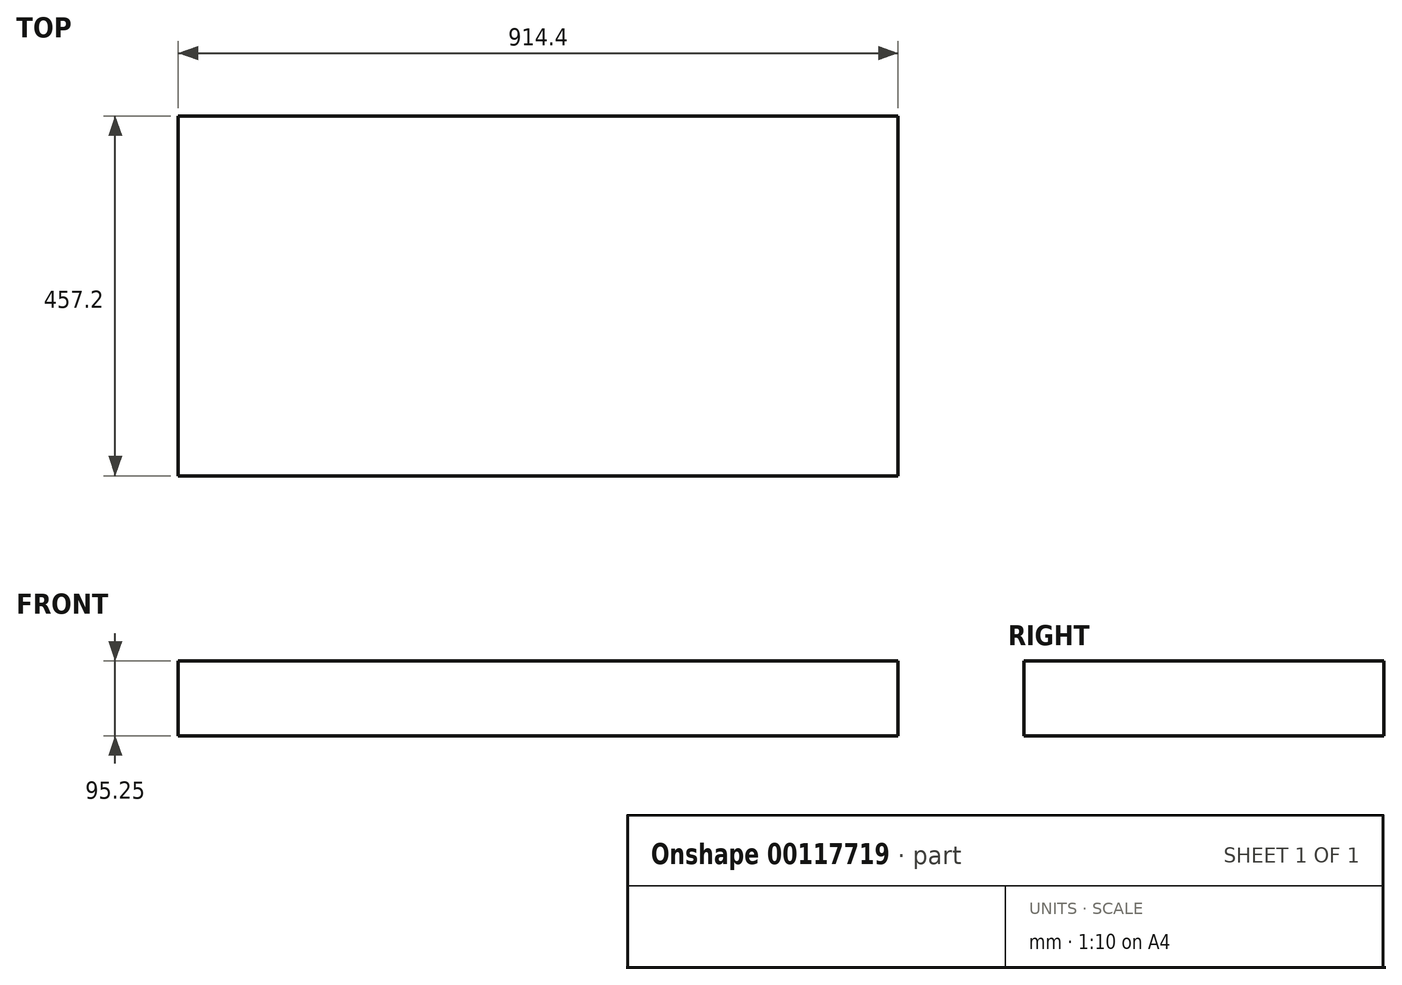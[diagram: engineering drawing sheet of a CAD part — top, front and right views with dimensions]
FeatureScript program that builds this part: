
annotation { "Feature Type Name" : "Feature", "Feature Type Description" : "" }
export const myFeature = defineFeature(function(context is Context, id is Id, definition is map)
    precondition{}
    {
        {
            var Q0;
            Q0=qCreatedBy(makeId("Top.planeOp"),FACE);
            var sketch = newSketch(context, id + "F0", { "sketchPlane" : qUnion([Q0])});
            skLineSegment(sketch, "E0.bottom", {"start": v(-467.76, 71.78) * mm, "end": v(446.64, 71.78) * mm});
            skLineSegment(sketch, "E0.top", {"start": v(-467.76, 43.2) * mm, "end": v(446.64, 43.2) * mm});
            skLineSegment(sketch, "E0.left", {"start": v(-467.76, 71.78) * mm, "end": v(-467.76, 43.2) * mm});
            skLineSegment(sketch, "E0.right", {"start": v(446.64, 71.78) * mm, "end": v(446.64, 43.2) * mm});
            skLineSegment(sketch, "E1.top", {"start": v(-467.76, 14.63) * mm, "end": v(446.64, 14.63) * mm});
            skLineSegment(sketch, "E1.left", {"start": v(-467.76, 43.2) * mm, "end": v(-467.76, 14.63) * mm});
            skLineSegment(sketch, "E1.right", {"start": v(446.64, 43.2) * mm, "end": v(446.64, 14.63) * mm});
            skLineSegment(sketch, "E2.top", {"start": v(-467.76, -13.94) * mm, "end": v(446.64, -13.94) * mm});
            skLineSegment(sketch, "E2.left", {"start": v(-467.76, 14.63) * mm, "end": v(-467.76, -13.94) * mm});
            skLineSegment(sketch, "E2.right", {"start": v(446.64, 14.63) * mm, "end": v(446.64, -13.94) * mm});
            skLineSegment(sketch, "E3.top", {"start": v(-467.76, -42.52) * mm, "end": v(446.64, -42.52) * mm});
            skLineSegment(sketch, "E3.left", {"start": v(-467.76, -13.94) * mm, "end": v(-467.76, -42.52) * mm});
            skLineSegment(sketch, "E3.right", {"start": v(446.64, -13.94) * mm, "end": v(446.64, -42.52) * mm});
            skLineSegment(sketch, "E4.top", {"start": v(-467.76, -71.1) * mm, "end": v(446.64, -71.1) * mm});
            skLineSegment(sketch, "E4.left", {"start": v(-467.76, -42.52) * mm, "end": v(-467.76, -71.1) * mm});
            skLineSegment(sketch, "E4.right", {"start": v(446.64, -42.52) * mm, "end": v(446.64, -71.1) * mm});
            skLineSegment(sketch, "E5.MirrorCS", {"start": v(-467.76, -128.24) * mm, "end": v(446.64, -128.24) * mm});
            skLineSegment(sketch, "E6.MirrorCS", {"start": v(-467.76, -156.82) * mm, "end": v(446.64, -156.82) * mm});
            skLineSegment(sketch, "E7.MirrorCS", {"start": v(-467.76, -99.67) * mm, "end": v(446.64, -99.67) * mm});
            skLineSegment(sketch, "E8.MirrorCS", {"start": v(-467.76, -185.4) * mm, "end": v(446.64, -185.4) * mm});
            skLineSegment(sketch, "E9.MirrorCS", {"start": v(446.64, -99.67) * mm, "end": v(446.64, -71.1) * mm});
            skLineSegment(sketch, "E10.MirrorCS", {"start": v(-467.76, -99.67) * mm, "end": v(-467.76, -71.1) * mm});
            skLineSegment(sketch, "E11.MirrorCS", {"start": v(-467.76, -156.82) * mm, "end": v(-467.76, -128.24) * mm});
            skLineSegment(sketch, "E12.MirrorCS", {"start": v(446.64, -185.4) * mm, "end": v(446.64, -156.82) * mm});
            skLineSegment(sketch, "E13.MirrorCS", {"start": v(-467.76, -185.4) * mm, "end": v(-467.76, -156.82) * mm});
            skLineSegment(sketch, "E14.MirrorCS", {"start": v(446.64, -213.97) * mm, "end": v(446.64, -185.4) * mm});
            skLineSegment(sketch, "E15.MirrorCS", {"start": v(-467.76, -213.97) * mm, "end": v(-467.76, -185.4) * mm});
            skLineSegment(sketch, "E16.MirrorCS", {"start": v(446.64, -128.24) * mm, "end": v(446.64, -99.67) * mm});
            skLineSegment(sketch, "E17.MirrorCS", {"start": v(-467.76, -128.24) * mm, "end": v(-467.76, -99.67) * mm});
            skLineSegment(sketch, "E18.MirrorCS", {"start": v(446.64, -156.82) * mm, "end": v(446.64, -128.24) * mm});
            skLineSegment(sketch, "E19.MirrorCS", {"start": v(-467.76, -213.97) * mm, "end": v(446.64, -213.97) * mm});
            skLineSegment(sketch, "E20.MirrorCS", {"start": v(-467.76, -242.54) * mm, "end": v(446.64, -242.54) * mm});
            skLineSegment(sketch, "E21.MirrorCS", {"start": v(-467.76, -213.97) * mm, "end": v(-467.76, -242.54) * mm});
            skLineSegment(sketch, "E22.MirrorCS", {"start": v(446.64, -213.97) * mm, "end": v(446.64, -242.54) * mm});
            skLineSegment(sketch, "E23.MirrorCS", {"start": v(-467.76, -242.54) * mm, "end": v(-467.76, -271.12) * mm});
            skLineSegment(sketch, "E24.MirrorCS", {"start": v(446.64, -242.54) * mm, "end": v(446.64, -271.12) * mm});
            skLineSegment(sketch, "E25", {"start": v(-467.76, -271.12) * mm, "end": v(446.64, -271.12) * mm});
            skLineSegment(sketch, "E26.MirrorCS", {"start": v(-467.76, -299.7) * mm, "end": v(446.64, -299.7) * mm});
            skLineSegment(sketch, "E27.MirrorCS", {"start": v(-467.76, -328.27) * mm, "end": v(-467.76, -299.7) * mm});
            skLineSegment(sketch, "E28.MirrorCS", {"start": v(-467.76, -328.27) * mm, "end": v(446.64, -328.27) * mm});
            skLineSegment(sketch, "E29.MirrorCS", {"start": v(-467.76, -299.7) * mm, "end": v(-467.76, -271.12) * mm});
            skLineSegment(sketch, "E30.MirrorCS", {"start": v(446.64, -328.27) * mm, "end": v(446.64, -299.7) * mm});
            skLineSegment(sketch, "E31.MirrorCS", {"start": v(446.64, -299.7) * mm, "end": v(446.64, -271.12) * mm});
            skLineSegment(sketch, "E32.MirrorCS", {"start": v(-467.76, -356.84) * mm, "end": v(446.64, -356.84) * mm});
            skLineSegment(sketch, "E33.MirrorCS", {"start": v(446.64, -328.27) * mm, "end": v(446.64, -356.84) * mm});
            skLineSegment(sketch, "E34.MirrorCS", {"start": v(-467.76, -328.27) * mm, "end": v(-467.76, -356.84) * mm});
            skLineSegment(sketch, "E35.MirrorCS", {"start": v(-467.76, -385.42) * mm, "end": v(446.64, -385.42) * mm});
            skLineSegment(sketch, "E36.MirrorCS", {"start": v(-467.76, -385.42) * mm, "end": v(-467.76, -356.84) * mm});
            skLineSegment(sketch, "E37.MirrorCS", {"start": v(446.64, -385.42) * mm, "end": v(446.64, -356.84) * mm});
            skSolve(sketch);
        }
        {
            var Q0;
            Q0 = qSketchRegion(id + "F0", true);
            extrude(context, id + "F1", {"entities" : qUnion([Q0]), "depth" : 95.25 * mm});
        }
    });
